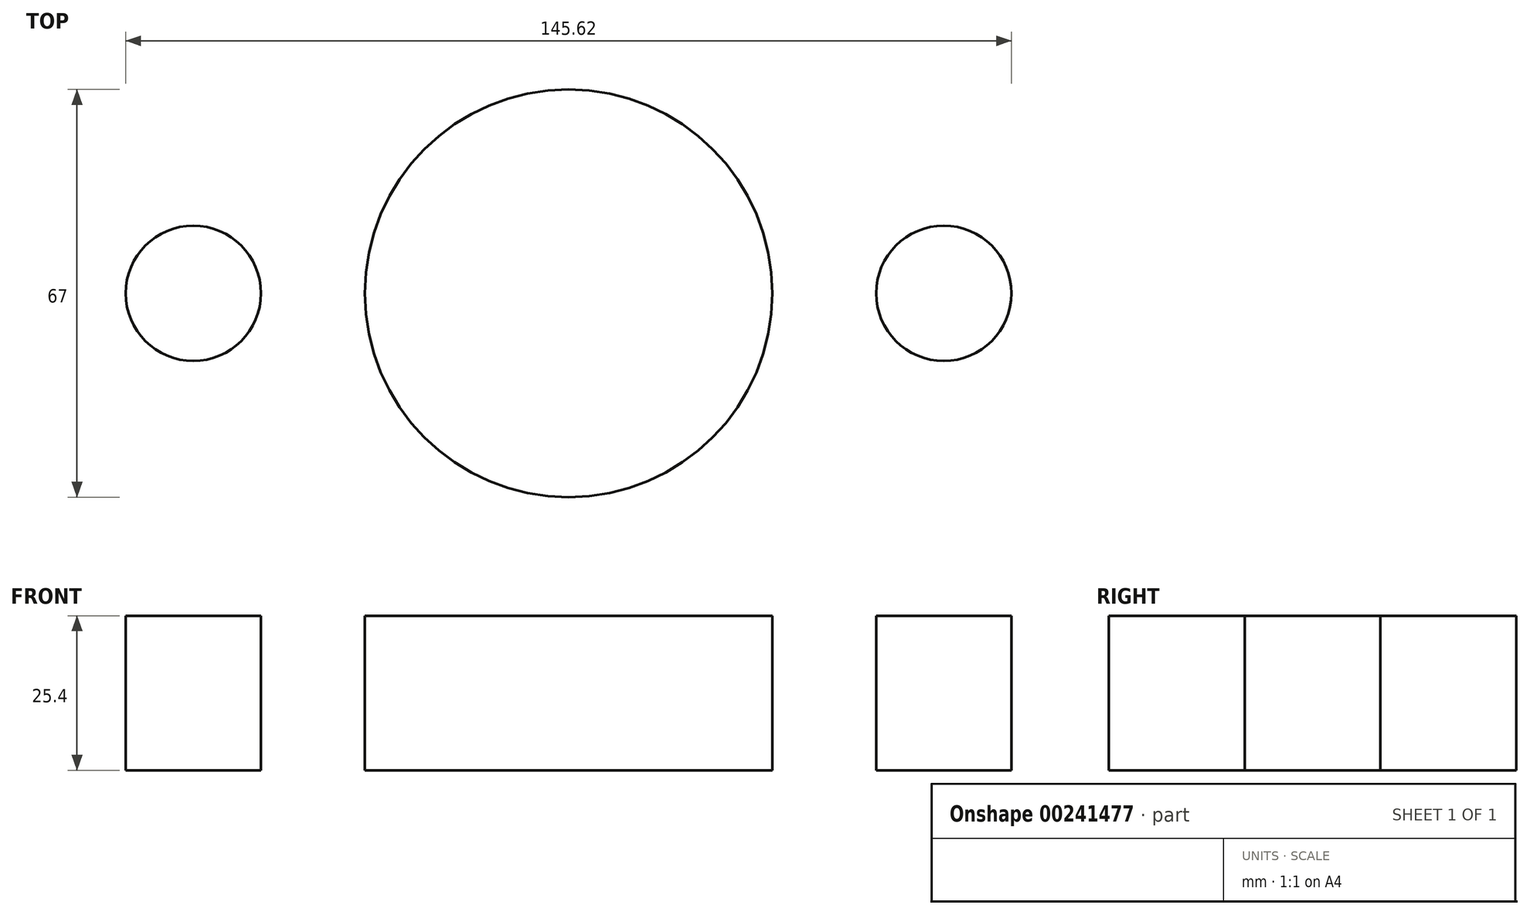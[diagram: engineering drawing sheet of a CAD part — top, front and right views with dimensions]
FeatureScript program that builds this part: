
annotation { "Feature Type Name" : "Feature", "Feature Type Description" : "" }
export const myFeature = defineFeature(function(context is Context, id is Id, definition is map)
    precondition{}
    {
        {
            var Q0;
            Q0=qCreatedBy(makeId("Top.planeOp"),FACE);
            var sketch = newSketch(context, id + "F0", { "sketchPlane" : qUnion([Q0])});
            skCircle(sketch, "E0", {"center": v(0, 0) * mm, "radius": 33.5 * mm});
            skCircle(sketch, "E1", {"center": v(-61.69, 0) * mm, "radius": 11.12 * mm});
            skCircle(sketch, "E2", {"center": v(61.69, 0) * mm, "radius": 11.12 * mm});
            skSolve(sketch);
        }
        {
            var Q0;
            Q0 = qSketchRegion(id + "F0", true);
            extrude(context, id + "F1", {"entities" : qUnion([Q0]), "depth" : 25.4 * mm});
        }
    });
